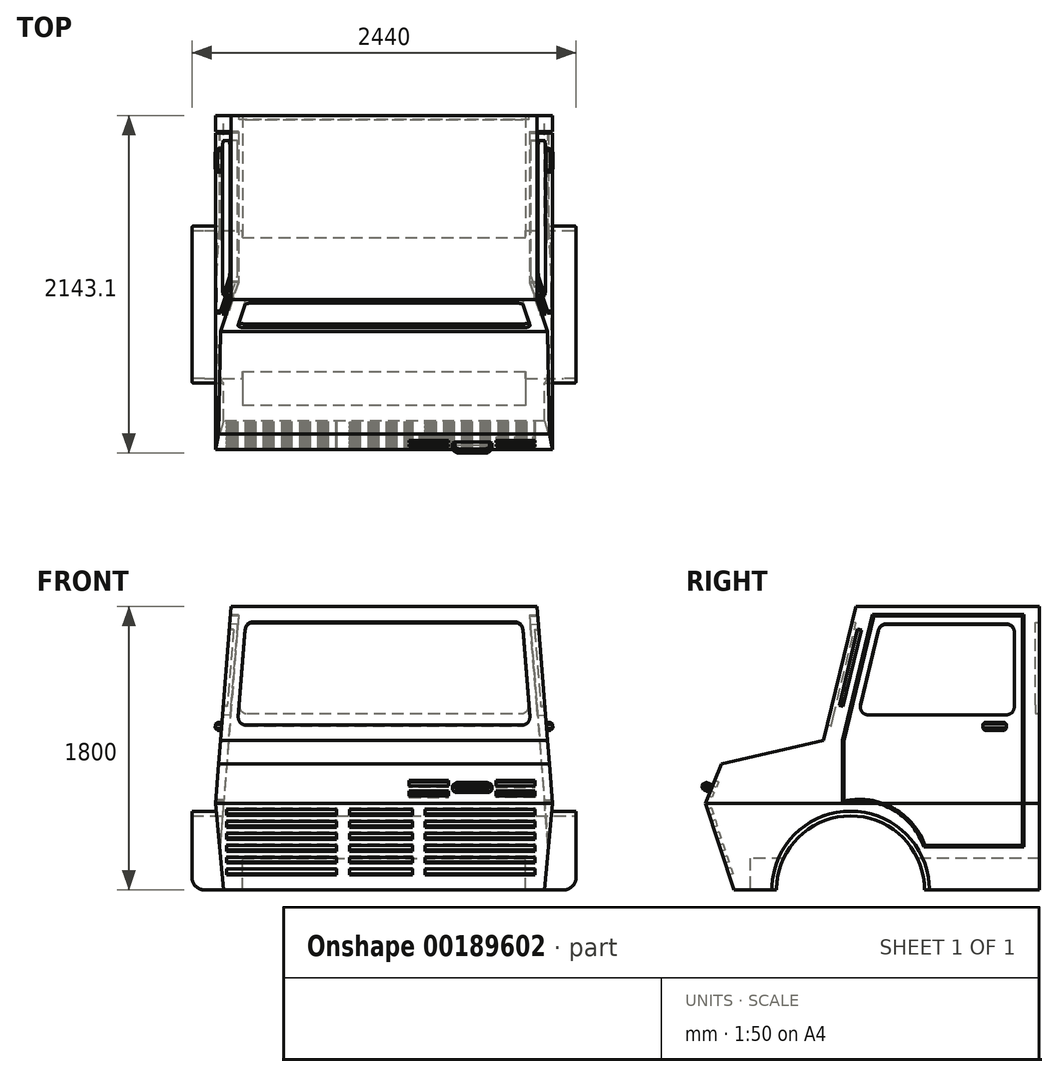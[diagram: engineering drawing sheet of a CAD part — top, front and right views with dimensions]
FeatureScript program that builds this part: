
annotation { "Feature Type Name" : "Feature", "Feature Type Description" : "" }
export const myFeature = defineFeature(function(context is Context, id is Id, definition is map)
    precondition{}
    {
        {
            var Q0;
            Q0=qCreatedBy(makeId("Right.planeOp"),FACE);
            var sketch = newSketch(context, id + "F0", { "sketchPlane" : qUnion([Q0])});
            skLineSegment(sketch, "E0", {"start": v(-687.2, -888.86) * mm, "end": v(-447.2, -888.86) * mm});
            skLineSegment(sketch, "E1", {"start": v(1252.8, -888.86) * mm, "end": v(1252.8, 911.14) * mm});
            skLineSegment(sketch, "E2", {"start": v(1252.8, 911.14) * mm, "end": v(86.04, 911.14) * mm});
            skLineSegment(sketch, "E3", {"start": v(86.04, 911.14) * mm, "end": v(-118.03, 61.14) * mm});
            skLineSegment(sketch, "E4", {"start": v(-118.03, 61.14) * mm, "end": v(-768.03, -88.86) * mm});
            skLineSegment(sketch, "E5", {"start": v(-768.03, -88.86) * mm, "end": v(-868.03, -338.86) * mm});
            skLineSegment(sketch, "E6", {"start": v(-868.03, -338.86) * mm, "end": v(-687.2, -888.86) * mm});
            skArc(sketch, "E7", {"start": v(552.8, -888.86) * mm, "mid": v(52.8, -388.86) * mm, "end": v(-447.2, -888.86) * mm});
            skLineSegment(sketch, "E8.trimOffspring", {"start": v(552.8, -888.86) * mm, "end": v(1252.8, -888.86) * mm});
            skLineSegment(sketch, "E9", {"start": v(-687.2, -888.86) * mm, "end": v(-687.2, 1285.93) * mm, "construction": true});
            skSolve(sketch);
        }
        {
            var Q0;
            Q0 = qSketchRegion(id + "F0", true);
            extrude(context, id + "F1", {"entities" : qUnion([Q0]), "depth" : 2140 * mm});
        }
        {
            var Q0;
            Q0=makeQuery(id+"F1.opExtrude","SWEPT_FACE",FACE,{"disambiguationData":[OSD([sQuery(id+"F0.wireOp",EDGE,"E1")])]});
            var sketch = newSketch(context, id + "F2", { "sketchPlane" : qUnion([Q0])});
            skLineSegment(sketch, "E10", {"start": v(-2140, -888.86) * mm, "end": v(-2090, -888.86) * mm});
            skLineSegment(sketch, "E11", {"start": v(-2090, -888.86) * mm, "end": v(-2140, -338.86) * mm});
            skLineSegment(sketch, "E12", {"start": v(-2140, -338.86) * mm, "end": v(-2040, 911.14) * mm});
            skLineSegment(sketch, "E13", {"start": v(-2040, 911.14) * mm, "end": v(-2140, 911.14) * mm});
            skLineSegment(sketch, "E14", {"start": v(-2140, 911.14) * mm, "end": v(-2140, -888.86) * mm});
            skLineSegment(sketch, "E15", {"start": v(-2090, -888.86) * mm, "end": v(-2140, -888.86) * mm});
            skLineSegment(sketch, "E16", {"start": v(0, -888.86) * mm, "end": v(-50, -888.86) * mm});
            skLineSegment(sketch, "E17", {"start": v(-50, -888.86) * mm, "end": v(0, -338.86) * mm});
            skLineSegment(sketch, "E18", {"start": v(0, -338.86) * mm, "end": v(-100, 911.14) * mm});
            skLineSegment(sketch, "E19", {"start": v(-100, 911.14) * mm, "end": v(0, 911.14) * mm});
            skLineSegment(sketch, "E20", {"start": v(0, 911.14) * mm, "end": v(0, -888.86) * mm});
            skSolve(sketch);
        }
        {
            var Q0;
            {var subQ0=sQuery(id+"F2.wireOp",EDGE,"E12");Q0=makeQuery(id+"F2.imprint","IMPRINT",FACE,{"disambiguationData":[TD([[makeQuery(id+"F2.imprint","IMPRINT",EDGE,{"derivedFrom":subQ0}),1.0]])]});}
            var Q1;
            {var subQ0=sQuery(id+"F2.wireOp",EDGE,"E11");Q1=makeQuery(id+"F2.imprint","IMPRINT",FACE,{"disambiguationData":[TD([[makeQuery(id+"F2.imprint","IMPRINT",EDGE,{"derivedFrom":subQ0}),1.0]])]});}
            var Q2;
            {var subQ0=sQuery(id+"F2.wireOp",EDGE,"E16");Q2=makeQuery(id+"F2.imprint","IMPRINT",FACE,{"disambiguationData":[TD([[makeQuery(id+"F2.imprint","IMPRINT",EDGE,{"derivedFrom":subQ0}),1.0]])]});}
            var Q3;
            {var subQ0=sQuery(id+"F2.wireOp",EDGE,"E18");Q3=makeQuery(id+"F2.imprint","IMPRINT",FACE,{"disambiguationData":[TD([[makeQuery(id+"F2.imprint","IMPRINT",EDGE,{"derivedFrom":subQ0}),-1.0]])]});}
            extrude(context, id + "F3", {"entities" : qUnion([Q0, Q1, Q2, Q3]), "operationType" : NewBodyOperationType.REMOVE, "oppositeDirection" : true, "depth" : 2500 * mm});
        }
        {
            var Q0;
            Q0=makeQuery(id+"F1.opExtrude","SWEPT_FACE",FACE,{"disambiguationData":[OSD([sQuery(id+"F0.wireOp",EDGE,"E6")])]});
            var sketch = newSketch(context, id + "F4", { "sketchPlane" : qUnion([Q0])});
            skLineSegment(sketch, "E21.bottom", {"start": v(70, -90.81) * mm, "end": v(770, -90.81) * mm});
            skLineSegment(sketch, "E21.top", {"start": v(70, -130.81) * mm, "end": v(770, -130.81) * mm});
            skLineSegment(sketch, "E21.left", {"start": v(70, -90.81) * mm, "end": v(70, -130.81) * mm});
            skLineSegment(sketch, "E21.right", {"start": v(770, -90.81) * mm, "end": v(770, -130.81) * mm});
            skLineSegment(sketch, "E22.bottom", {"start": v(850, -90.81) * mm, "end": v(1250, -90.81) * mm});
            skLineSegment(sketch, "E22.top", {"start": v(850, -130.81) * mm, "end": v(1250, -130.81) * mm});
            skLineSegment(sketch, "E22.left", {"start": v(850, -90.81) * mm, "end": v(850, -130.81) * mm});
            skLineSegment(sketch, "E22.right", {"start": v(1250, -90.81) * mm, "end": v(1250, -130.81) * mm});
            skLineSegment(sketch, "E23.bottom", {"start": v(1330, -90.81) * mm, "end": v(2030, -90.81) * mm});
            skLineSegment(sketch, "E23.top", {"start": v(1330, -130.81) * mm, "end": v(2030, -130.81) * mm});
            skLineSegment(sketch, "E23.left", {"start": v(1330, -90.81) * mm, "end": v(1330, -130.81) * mm});
            skLineSegment(sketch, "E23.right", {"start": v(2030, -90.81) * mm, "end": v(2030, -130.81) * mm});
            skLineSegment(sketch, "E24.bottom", {"start": v(70, -170.81) * mm, "end": v(770, -170.81) * mm});
            skLineSegment(sketch, "E24.top", {"start": v(70, -210.81) * mm, "end": v(770, -210.81) * mm});
            skLineSegment(sketch, "E24.left", {"start": v(70, -170.81) * mm, "end": v(70, -210.81) * mm});
            skLineSegment(sketch, "E24.right", {"start": v(770, -170.81) * mm, "end": v(770, -210.81) * mm});
            skLineSegment(sketch, "E25.bottom", {"start": v(850, -170.81) * mm, "end": v(1250, -170.81) * mm});
            skLineSegment(sketch, "E25.top", {"start": v(850, -210.81) * mm, "end": v(1250, -210.81) * mm});
            skLineSegment(sketch, "E25.left", {"start": v(850, -170.81) * mm, "end": v(850, -210.81) * mm});
            skLineSegment(sketch, "E25.right", {"start": v(1250, -170.81) * mm, "end": v(1250, -210.81) * mm});
            skLineSegment(sketch, "E26.bottom", {"start": v(1330, -170.81) * mm, "end": v(2030, -170.81) * mm});
            skLineSegment(sketch, "E26.top", {"start": v(1330, -210.81) * mm, "end": v(2030, -210.81) * mm});
            skLineSegment(sketch, "E26.left", {"start": v(1330, -170.81) * mm, "end": v(1330, -210.81) * mm});
            skLineSegment(sketch, "E26.right", {"start": v(2030, -170.81) * mm, "end": v(2030, -210.81) * mm});
            skLineSegment(sketch, "E27.bottom", {"start": v(70, -250.81) * mm, "end": v(770, -250.81) * mm});
            skLineSegment(sketch, "E27.top", {"start": v(70, -290.81) * mm, "end": v(770, -290.81) * mm});
            skLineSegment(sketch, "E27.left", {"start": v(70, -250.81) * mm, "end": v(70, -290.81) * mm});
            skLineSegment(sketch, "E27.right", {"start": v(770, -250.81) * mm, "end": v(770, -290.81) * mm});
            skLineSegment(sketch, "E28.bottom", {"start": v(850, -250.81) * mm, "end": v(1250, -250.81) * mm});
            skLineSegment(sketch, "E28.top", {"start": v(850, -290.81) * mm, "end": v(1250, -290.81) * mm});
            skLineSegment(sketch, "E28.left", {"start": v(850, -250.81) * mm, "end": v(850, -290.81) * mm});
            skLineSegment(sketch, "E28.right", {"start": v(1250, -250.81) * mm, "end": v(1250, -290.81) * mm});
            skLineSegment(sketch, "E29.bottom", {"start": v(1330, -250.81) * mm, "end": v(2030, -250.81) * mm});
            skLineSegment(sketch, "E29.top", {"start": v(1330, -290.81) * mm, "end": v(2030, -290.81) * mm});
            skLineSegment(sketch, "E29.left", {"start": v(1330, -250.81) * mm, "end": v(1330, -290.81) * mm});
            skLineSegment(sketch, "E29.right", {"start": v(2030, -250.81) * mm, "end": v(2030, -290.81) * mm});
            skLineSegment(sketch, "E30.bottom", {"start": v(70, -330.81) * mm, "end": v(770, -330.81) * mm});
            skLineSegment(sketch, "E30.top", {"start": v(70, -370.81) * mm, "end": v(770, -370.81) * mm});
            skLineSegment(sketch, "E30.left", {"start": v(70, -330.81) * mm, "end": v(70, -370.81) * mm});
            skLineSegment(sketch, "E30.right", {"start": v(770, -330.81) * mm, "end": v(770, -370.81) * mm});
            skLineSegment(sketch, "E31.bottom", {"start": v(850, -330.81) * mm, "end": v(1250, -330.81) * mm});
            skLineSegment(sketch, "E31.top", {"start": v(850, -370.81) * mm, "end": v(1250, -370.81) * mm});
            skLineSegment(sketch, "E31.left", {"start": v(850, -330.81) * mm, "end": v(850, -370.81) * mm});
            skLineSegment(sketch, "E31.right", {"start": v(1250, -330.81) * mm, "end": v(1250, -370.81) * mm});
            skLineSegment(sketch, "E32.bottom", {"start": v(1330, -330.81) * mm, "end": v(2030, -330.81) * mm});
            skLineSegment(sketch, "E32.top", {"start": v(1330, -370.81) * mm, "end": v(2030, -370.81) * mm});
            skLineSegment(sketch, "E32.left", {"start": v(1330, -330.81) * mm, "end": v(1330, -370.81) * mm});
            skLineSegment(sketch, "E32.right", {"start": v(2030, -330.81) * mm, "end": v(2030, -370.81) * mm});
            skLineSegment(sketch, "E33.bottom", {"start": v(70, -410.81) * mm, "end": v(770, -410.81) * mm});
            skLineSegment(sketch, "E33.top", {"start": v(70, -450.81) * mm, "end": v(770, -450.81) * mm});
            skLineSegment(sketch, "E33.left", {"start": v(70, -410.81) * mm, "end": v(70, -450.81) * mm});
            skLineSegment(sketch, "E33.right", {"start": v(770, -410.81) * mm, "end": v(770, -450.81) * mm});
            skLineSegment(sketch, "E34.bottom", {"start": v(850, -410.81) * mm, "end": v(1250, -410.81) * mm});
            skLineSegment(sketch, "E34.top", {"start": v(850, -450.81) * mm, "end": v(1250, -450.81) * mm});
            skLineSegment(sketch, "E34.left", {"start": v(850, -410.81) * mm, "end": v(850, -450.81) * mm});
            skLineSegment(sketch, "E34.right", {"start": v(1250, -410.81) * mm, "end": v(1250, -450.81) * mm});
            skLineSegment(sketch, "E35.bottom", {"start": v(1330, -410.81) * mm, "end": v(2030, -410.81) * mm});
            skLineSegment(sketch, "E35.top", {"start": v(1330, -450.81) * mm, "end": v(2030, -450.81) * mm});
            skLineSegment(sketch, "E35.left", {"start": v(1330, -410.81) * mm, "end": v(1330, -450.81) * mm});
            skLineSegment(sketch, "E35.right", {"start": v(2030, -410.81) * mm, "end": v(2030, -450.81) * mm});
            skLineSegment(sketch, "E36.bottom", {"start": v(70, -490.81) * mm, "end": v(770, -490.81) * mm});
            skLineSegment(sketch, "E36.top", {"start": v(70, -530.81) * mm, "end": v(770, -530.81) * mm});
            skLineSegment(sketch, "E36.left", {"start": v(70, -490.81) * mm, "end": v(70, -530.81) * mm});
            skLineSegment(sketch, "E36.right", {"start": v(770, -490.81) * mm, "end": v(770, -530.81) * mm});
            skLineSegment(sketch, "E37.bottom", {"start": v(850, -490.81) * mm, "end": v(1250, -490.81) * mm});
            skLineSegment(sketch, "E37.top", {"start": v(850, -530.81) * mm, "end": v(1250, -530.81) * mm});
            skLineSegment(sketch, "E37.left", {"start": v(850, -490.81) * mm, "end": v(850, -530.81) * mm});
            skLineSegment(sketch, "E37.right", {"start": v(1250, -490.81) * mm, "end": v(1250, -530.81) * mm});
            skLineSegment(sketch, "E38.bottom", {"start": v(1330, -490.81) * mm, "end": v(2030, -490.81) * mm});
            skLineSegment(sketch, "E38.top", {"start": v(1330, -530.81) * mm, "end": v(2030, -530.81) * mm});
            skLineSegment(sketch, "E38.left", {"start": v(1330, -490.81) * mm, "end": v(1330, -530.81) * mm});
            skLineSegment(sketch, "E38.right", {"start": v(2030, -490.81) * mm, "end": v(2030, -530.81) * mm});
            skSolve(sketch);
        }
        {
            var Q0;
            Q0=makeQuery(id+"F4.imprint","IMPRINT",FACE,{"disambiguationData":[TD([[makeQuery(id+"F4.imprint","IMPRINT",EDGE,{"derivedFrom":sQuery(id+"F4.wireOp",EDGE,"E22.bottom")}),-1.0]])]});
            var Q1;
            Q1=makeQuery(id+"F4.imprint","IMPRINT",FACE,{"disambiguationData":[TD([[makeQuery(id+"F4.imprint","IMPRINT",EDGE,{"derivedFrom":sQuery(id+"F4.wireOp",EDGE,"E23.bottom")}),-1.0]])]});
            var Q2;
            Q2=makeQuery(id+"F4.imprint","IMPRINT",FACE,{"disambiguationData":[TD([[makeQuery(id+"F4.imprint","IMPRINT",EDGE,{"derivedFrom":sQuery(id+"F4.wireOp",EDGE,"E26.bottom")}),-1.0]])]});
            var Q3;
            Q3=makeQuery(id+"F4.imprint","IMPRINT",FACE,{"disambiguationData":[TD([[makeQuery(id+"F4.imprint","IMPRINT",EDGE,{"derivedFrom":sQuery(id+"F4.wireOp",EDGE,"E25.bottom")}),-1.0]])]});
            var Q4;
            Q4=makeQuery(id+"F4.imprint","IMPRINT",FACE,{"disambiguationData":[TD([[makeQuery(id+"F4.imprint","IMPRINT",EDGE,{"derivedFrom":sQuery(id+"F4.wireOp",EDGE,"E24.bottom")}),-1.0]])]});
            var Q5;
            Q5=makeQuery(id+"F4.imprint","IMPRINT",FACE,{"disambiguationData":[TD([[makeQuery(id+"F4.imprint","IMPRINT",EDGE,{"derivedFrom":sQuery(id+"F4.wireOp",EDGE,"E21.bottom")}),-1.0]])]});
            var Q6;
            Q6=makeQuery(id+"F4.imprint","IMPRINT",FACE,{"disambiguationData":[TD([[makeQuery(id+"F4.imprint","IMPRINT",EDGE,{"derivedFrom":sQuery(id+"F4.wireOp",EDGE,"E27.bottom")}),-1.0]])]});
            var Q7;
            Q7=makeQuery(id+"F4.imprint","IMPRINT",FACE,{"disambiguationData":[TD([[makeQuery(id+"F4.imprint","IMPRINT",EDGE,{"derivedFrom":sQuery(id+"F4.wireOp",EDGE,"E28.bottom")}),-1.0]])]});
            var Q8;
            Q8=makeQuery(id+"F4.imprint","IMPRINT",FACE,{"disambiguationData":[TD([[makeQuery(id+"F4.imprint","IMPRINT",EDGE,{"derivedFrom":sQuery(id+"F4.wireOp",EDGE,"E29.bottom")}),-1.0]])]});
            var Q9;
            Q9=makeQuery(id+"F4.imprint","IMPRINT",FACE,{"disambiguationData":[TD([[makeQuery(id+"F4.imprint","IMPRINT",EDGE,{"derivedFrom":sQuery(id+"F4.wireOp",EDGE,"E32.bottom")}),-1.0]])]});
            var Q10;
            Q10=makeQuery(id+"F4.imprint","IMPRINT",FACE,{"disambiguationData":[TD([[makeQuery(id+"F4.imprint","IMPRINT",EDGE,{"derivedFrom":sQuery(id+"F4.wireOp",EDGE,"E31.bottom")}),-1.0]])]});
            var Q11;
            Q11=makeQuery(id+"F4.imprint","IMPRINT",FACE,{"disambiguationData":[TD([[makeQuery(id+"F4.imprint","IMPRINT",EDGE,{"derivedFrom":sQuery(id+"F4.wireOp",EDGE,"E30.bottom")}),-1.0]])]});
            var Q12;
            Q12=makeQuery(id+"F4.imprint","IMPRINT",FACE,{"disambiguationData":[TD([[makeQuery(id+"F4.imprint","IMPRINT",EDGE,{"derivedFrom":sQuery(id+"F4.wireOp",EDGE,"E33.bottom")}),-1.0]])]});
            var Q13;
            Q13=makeQuery(id+"F4.imprint","IMPRINT",FACE,{"disambiguationData":[TD([[makeQuery(id+"F4.imprint","IMPRINT",EDGE,{"derivedFrom":sQuery(id+"F4.wireOp",EDGE,"E34.bottom")}),-1.0]])]});
            var Q14;
            Q14=makeQuery(id+"F4.imprint","IMPRINT",FACE,{"disambiguationData":[TD([[makeQuery(id+"F4.imprint","IMPRINT",EDGE,{"derivedFrom":sQuery(id+"F4.wireOp",EDGE,"E35.bottom")}),-1.0]])]});
            var Q15;
            Q15=makeQuery(id+"F4.imprint","IMPRINT",FACE,{"disambiguationData":[TD([[makeQuery(id+"F4.imprint","IMPRINT",EDGE,{"derivedFrom":sQuery(id+"F4.wireOp",EDGE,"E37.bottom")}),-1.0]])]});
            var Q16;
            Q16=makeQuery(id+"F4.imprint","IMPRINT",FACE,{"disambiguationData":[TD([[makeQuery(id+"F4.imprint","IMPRINT",EDGE,{"derivedFrom":sQuery(id+"F4.wireOp",EDGE,"E38.bottom")}),-1.0]])]});
            var Q17;
            Q17=makeQuery(id+"F4.imprint","IMPRINT",FACE,{"disambiguationData":[TD([[makeQuery(id+"F4.imprint","IMPRINT",EDGE,{"derivedFrom":sQuery(id+"F4.wireOp",EDGE,"E36.bottom")}),-1.0]])]});
            extrude(context, id + "F5", {"entities" : qUnion([Q0, Q1, Q2, Q3, Q4, Q5, Q6, Q7, Q8, Q9, Q10, Q11, Q12, Q13, Q14, Q15, Q16, Q17]), "operationType" : NewBodyOperationType.REMOVE, "oppositeDirection" : true, "depth" : 25 * mm});
        }
        {
            var Q0;
            Q0=makeQuery(id+"F1.opExtrude","SWEPT_FACE",FACE,{"disambiguationData":[OSD([sQuery(id+"F0.wireOp",EDGE,"E3")])]});
            var sketch = newSketch(context, id + "F6", { "sketchPlane" : qUnion([Q0])});
            skLineSegment(sketch, "E39", {"start": v(188.94, 759.93) * mm, "end": v(144.27, 185.78) * mm});
            skLineSegment(sketch, "E40", {"start": v(194.12, 131.9) * mm, "end": v(1945.88, 131.9) * mm});
            skLineSegment(sketch, "E41", {"start": v(1995.73, 185.78) * mm, "end": v(1951.06, 759.93) * mm});
            skLineSegment(sketch, "E42", {"start": v(1901.22, 806.05) * mm, "end": v(238.78, 806.05) * mm});
            skPoint(sketch, "E43.visualSharp", {"position": v(140.08, 131.9) * mm});
            skArc(sketch, "E43.filletArc", {"start": v(144.27, 185.78) * mm, "mid": v(157.42, 147.94) * mm, "end": v(194.12, 131.9) * mm});
            skPoint(sketch, "E44.visualSharp", {"position": v(1999.92, 131.9) * mm});
            skArc(sketch, "E44.filletArc", {"start": v(1945.88, 131.9) * mm, "mid": v(1982.58, 147.94) * mm, "end": v(1995.73, 185.78) * mm});
            skPoint(sketch, "E45.visualSharp", {"position": v(1947.48, 806.05) * mm});
            skArc(sketch, "E45.filletArc", {"start": v(1951.06, 759.93) * mm, "mid": v(1935.17, 792.75) * mm, "end": v(1901.22, 806.05) * mm});
            skPoint(sketch, "E46.visualSharp", {"position": v(192.52, 806.05) * mm});
            skArc(sketch, "E46.filletArc", {"start": v(238.78, 806.05) * mm, "mid": v(204.83, 792.75) * mm, "end": v(188.94, 759.93) * mm});
            skSolve(sketch);
        }
        {
            var Q0;
            Q0=makeQuery(id+"F6.imprint","IMPRINT",FACE,{"disambiguationData":[TD([[makeQuery(id+"F6.imprint","IMPRINT",EDGE,{"derivedFrom":sQuery(id+"F6.wireOp",EDGE,"6I6eG5J9-oO44-mDBK-8rPG-g7Z5jDPBqrvn")}),-1.0]])]});
            var Q1;
            Q1=makeQuery(id+"F6.imprint","IMPRINT",FACE,{"disambiguationData":[TD([[makeQuery(id+"F6.imprint","IMPRINT",EDGE,{"derivedFrom":sQuery(id+"F6.wireOp",EDGE,"E39")}),1.0]])]});
            extrude(context, id + "F7", {"entities" : qUnion([Q0, Q1]), "operationType" : NewBodyOperationType.REMOVE, "oppositeDirection" : true, "depth" : 25 * mm});
        }
        {
            var Q0;
            Q0=makeQuery(id+"F3.boolean.opBoolean","COPY",FACE,{"derivedFrom":makeQuery(id+"F3.opExtrude","SWEPT_FACE",FACE,{"disambiguationData":[OSD([sQuery(id+"F2.wireOp",EDGE,"E12")])]})});
            var sketch = newSketch(context, id + "F8", { "sketchPlane" : qUnion([Q0])});
            skLineSegment(sketch, "E47", {"start": v(1152.8, 695.56) * mm, "end": v(192.4, 695.56) * mm});
            skLineSegment(sketch, "E48", {"start": v(192.4, 695.56) * mm, "end": v(0, -108.43) * mm});
            skLineSegment(sketch, "E49", {"start": v(0, -108.43) * mm, "end": v(0, -508.43) * mm});
            skArc(sketch, "E50", {"start": v(517.8, -782.7) * mm, "mid": v(312.84, -543.72) * mm, "end": v(0, -508.43) * mm});
            skLineSegment(sketch, "E51", {"start": v(517.8, -782.7) * mm, "end": v(1152.8, -782.7) * mm});
            skLineSegment(sketch, "E52", {"start": v(1152.8, 695.56) * mm, "end": v(1152.8, -782.7) * mm});
            skLineSegment(sketch, "E53", {"start": v(1142.8, 685.56) * mm, "end": v(200.3, 685.56) * mm});
            skLineSegment(sketch, "E54", {"start": v(200.3, 685.56) * mm, "end": v(10, -109.61) * mm});
            skLineSegment(sketch, "E55", {"start": v(10, -109.61) * mm, "end": v(10, -495.6) * mm});
            skArc(sketch, "E56", {"start": v(524.84, -772.7) * mm, "mid": v(320.1, -536.26) * mm, "end": v(10, -495.6) * mm});
            skLineSegment(sketch, "E57", {"start": v(524.84, -772.7) * mm, "end": v(1142.8, -772.7) * mm});
            skLineSegment(sketch, "E58", {"start": v(1142.8, 685.56) * mm, "end": v(1142.8, -772.7) * mm});
            skPoint(sketch, "E59.visualSharp", {"position": v(-103.75, -97.36) * mm});
            skLineSegment(sketch, "E60", {"start": v(1042.8, 635.56) * mm, "end": v(279.18, 635.56) * mm});
            skLineSegment(sketch, "E61", {"start": v(230.56, 597.2) * mm, "end": v(115.69, 117.2) * mm});
            skLineSegment(sketch, "E62", {"start": v(164.32, 55.56) * mm, "end": v(1042.8, 55.56) * mm});
            skLineSegment(sketch, "E63", {"start": v(1092.8, 105.56) * mm, "end": v(1092.8, 585.56) * mm});
            skPoint(sketch, "E64.visualSharp", {"position": v(239.74, 635.56) * mm});
            skArc(sketch, "E64.filletArc", {"start": v(279.18, 635.56) * mm, "mid": v(248.22, 624.81) * mm, "end": v(230.56, 597.2) * mm});
            skPoint(sketch, "E65.visualSharp", {"position": v(100.94, 55.56) * mm});
            skArc(sketch, "E65.filletArc", {"start": v(115.69, 117.2) * mm, "mid": v(125.06, 74.6) * mm, "end": v(164.32, 55.56) * mm});
            skPoint(sketch, "E66.visualSharp", {"position": v(1092.8, 55.56) * mm});
            skArc(sketch, "E66.filletArc", {"start": v(1042.8, 55.56) * mm, "mid": v(1078.15, 70.2) * mm, "end": v(1092.8, 105.56) * mm});
            skPoint(sketch, "E67.visualSharp", {"position": v(1092.8, 635.56) * mm});
            skArc(sketch, "E67.filletArc", {"start": v(1092.8, 585.56) * mm, "mid": v(1078.15, 620.92) * mm, "end": v(1042.8, 635.56) * mm});
            skSolve(sketch);
        }
        {
            var Q0;
            {var subQ9=sQuery(id+"F8.wireOp",EDGE,"E47");Q0=makeQuery(id+"F8.imprint","IMPRINT",FACE,{"disambiguationData":[TD([[makeQuery(id+"F8.imprint","IMPRINT",EDGE,{"derivedFrom":subQ9}),1.0]])]});}
            var Q1;
            {var subQ1=sQuery(id+"F8.wireOp",EDGE,"E51");Q1=makeQuery(id+"F8.imprint","IMPRINT",FACE,{"disambiguationData":[TD([[makeQuery(id+"F8.imprint","IMPRINT",EDGE,{"derivedFrom":subQ1}),1.0]])]});}
            var Q2;
            Q2=makeQuery(id+"F8.imprint","IMPRINT",FACE,{"disambiguationData":[TD([[makeQuery(id+"F8.imprint","IMPRINT",EDGE,{"derivedFrom":sQuery(id+"F8.wireOp",EDGE,"RXpK4xbC-jTpL-yFPa-w4cw-NWwqhQofK6yF")}),1.0]])]});
            var Q3;
            Q3=makeQuery(id+"F8.imprint","IMPRINT",FACE,{"disambiguationData":[TD([[makeQuery(id+"F8.imprint","IMPRINT",EDGE,{"derivedFrom":sQuery(id+"F8.wireOp",EDGE,"E60")}),1.0]])]});
            extrude(context, id + "F9", {"entities" : qUnion([Q0, Q1, Q2, Q3]), "operationType" : NewBodyOperationType.REMOVE, "oppositeDirection" : true, "depth" : 50 * mm});
        }
        {
            var Q0;
            Q0=makeQuery(id+"F3.boolean.opBoolean","COPY",FACE,{"derivedFrom":makeQuery(id+"F3.opExtrude","SWEPT_FACE",FACE,{"disambiguationData":[OSD([sQuery(id+"F2.wireOp",EDGE,"E18")])]})});
            var sketch = newSketch(context, id + "F10", { "sketchPlane" : qUnion([Q0])});
            skLineSegment(sketch, "E68.MirrorCS", {"start": v(-517.74, -612.04) * mm, "end": v(-1152.8, -612.04) * mm});
            skLineSegment(sketch, "E69.MirrorCS", {"start": v(-1152.8, 866.21) * mm, "end": v(-1152.8, -612.04) * mm});
            skLineSegment(sketch, "E70.MirrorCS", {"start": v(-1142.8, 856.21) * mm, "end": v(-200.2, 856.21) * mm});
            skLineSegment(sketch, "E71.MirrorCS", {"start": v(-200.2, 856.21) * mm, "end": v(-9.92, 61.04) * mm});
            skLineSegment(sketch, "E72.MirrorCS", {"start": v(-9.92, 61.04) * mm, "end": v(-9.92, -324.94) * mm});
            skArc(sketch, "E73.MirrorCS", {"start": v(-524.8, -602.04) * mm, "mid": v(-320.04, -365.6) * mm, "end": v(-9.92, -324.94) * mm});
            skLineSegment(sketch, "E74.MirrorCS", {"start": v(-524.8, -602.04) * mm, "end": v(-1142.8, -602.04) * mm});
            skLineSegment(sketch, "E75.MirrorCS", {"start": v(-1142.8, 856.21) * mm, "end": v(-1142.8, -602.04) * mm});
            skPoint(sketch, "E76.MirrorP", {"position": v(142.86, 102.71) * mm});
            skLineSegment(sketch, "E77.MirrorCS", {"start": v(-1152.8, 866.21) * mm, "end": v(-192.32, 866.21) * mm});
            skLineSegment(sketch, "E78.MirrorCS", {"start": v(-192.32, 866.21) * mm, "end": v(0.08, 62.22) * mm});
            skLineSegment(sketch, "E79.MirrorCS", {"start": v(0.08, 62.22) * mm, "end": v(0.08, -337.78) * mm});
            skArc(sketch, "E80.MirrorCS", {"start": v(-517.74, -612.04) * mm, "mid": v(-312.77, -373.05) * mm, "end": v(0.08, -337.78) * mm});
            skLineSegment(sketch, "E81", {"start": v(-1092.8, 756.21) * mm, "end": v(-1092.8, 276.21) * mm});
            skLineSegment(sketch, "E82", {"start": v(-1042.8, 226.21) * mm, "end": v(-164.23, 226.21) * mm});
            skLineSegment(sketch, "E83", {"start": v(-115.6, 287.85) * mm, "end": v(-230.47, 767.85) * mm});
            skLineSegment(sketch, "E84", {"start": v(-279.1, 806.21) * mm, "end": v(-1042.8, 806.21) * mm});
            skPoint(sketch, "E85.visualSharp", {"position": v(-1092.8, 806.21) * mm});
            skArc(sketch, "E85.filletArc", {"start": v(-1042.8, 806.21) * mm, "mid": v(-1078.15, 791.57) * mm, "end": v(-1092.8, 756.21) * mm});
            skPoint(sketch, "E86.visualSharp", {"position": v(-239.65, 806.21) * mm});
            skArc(sketch, "E86.filletArc", {"start": v(-230.47, 767.85) * mm, "mid": v(-248.13, 795.47) * mm, "end": v(-279.1, 806.21) * mm});
            skPoint(sketch, "E87.visualSharp", {"position": v(-1092.8, 226.21) * mm});
            skArc(sketch, "E87.filletArc", {"start": v(-1092.8, 276.21) * mm, "mid": v(-1078.15, 240.86) * mm, "end": v(-1042.8, 226.21) * mm});
            skPoint(sketch, "E88.visualSharp", {"position": v(-100.86, 226.21) * mm});
            skArc(sketch, "E88.filletArc", {"start": v(-164.23, 226.21) * mm, "mid": v(-124.98, 245.25) * mm, "end": v(-115.6, 287.85) * mm});
            skSolve(sketch);
        }
        {
            var Q0;
            Q0 = qSketchRegion(id + "F10", true);
            var Q1;
            Q1=makeQuery(id+"F10.imprint","IMPRINT",FACE,{"disambiguationData":[TD([[makeQuery(id+"F10.imprint","IMPRINT",EDGE,{"derivedFrom":sQuery(id+"F10.wireOp",EDGE,"E81")}),1.0]])]});
            extrude(context, id + "F11", {"entities" : qUnion([Q0, Q1]), "operationType" : NewBodyOperationType.REMOVE, "oppositeDirection" : true, "depth" : 50 * mm});
        }
        {
            var Q0;
            Q0=qCreatedBy(makeId("Right.planeOp"),FACE);
            var sketch = newSketch(context, id + "F12", { "sketchPlane" : qUnion([Q0])});
            skArc(sketch, "E89", {"start": v(552.8, -888.86) * mm, "mid": v(52.8, -388.86) * mm, "end": v(-447.2, -888.86) * mm});
            skArc(sketch, "E90", {"start": v(522.8, -888.86) * mm, "mid": v(52.8, -418.86) * mm, "end": v(-417.2, -888.86) * mm});
            skLineSegment(sketch, "E91", {"start": v(1160.67, -888.86) * mm, "end": v(-584.2, -888.86) * mm, "construction": true});
            skLineSegment(sketch, "E92", {"start": v(552.8, -888.86) * mm, "end": v(522.8, -888.86) * mm});
            skLineSegment(sketch, "E93", {"start": v(-417.2, -888.86) * mm, "end": v(-447.2, -888.86) * mm});
            skSolve(sketch);
        }
        {
            var Q0;
            Q0=makeQuery(id+"F12.imprint","IMPRINT",FACE,{"disambiguationData":[TD([[makeQuery(id+"F12.imprint","IMPRINT",EDGE,{"derivedFrom":sQuery(id+"F12.wireOp",EDGE,"E89")}),1.0]])]});
            extrude(context, id + "F13", {"entities" : qUnion([Q0]), "operationType" : NewBodyOperationType.ADD, "oppositeDirection" : true, "depth" : 150 * mm, "hasSecondDirection" : true, "secondDirectionOppositeDirection" : false, "secondDirectionDepth" : 2290 * mm});
        }
        {
            var Q0;
            Q0=makeQuery(id+"F13.opExtrude","CAP_EDGE",EDGE,{"disambiguationData":[OSD([sQuery(id+"F12.wireOp",EDGE,"E93")])],"isStart":false});
            var Q1;
            Q1=makeQuery(id+"F13.opExtrude","CAP_EDGE",EDGE,{"disambiguationData":[OSD([sQuery(id+"F12.wireOp",EDGE,"E92")])],"isStart":false});
            var Q2;
            Q2=makeQuery(id+"F13.opExtrude","CAP_EDGE",EDGE,{"disambiguationData":[OSD([sQuery(id+"F12.wireOp",EDGE,"E93")])],"isStart":true});
            var Q3;
            Q3=makeQuery(id+"F13.opExtrude","CAP_EDGE",EDGE,{"disambiguationData":[OSD([sQuery(id+"F12.wireOp",EDGE,"E92")])],"isStart":true});
            var Q4;
            Q4=makeQuery(id+"F3.boolean.opBoolean","COPY",EDGE,{"derivedFrom":makeQuery(id+"F3.opExtrude","SWEPT_EDGE",EDGE,{"disambiguationData":[OSD([sQuery(id+"F0.wireOp",EDGE,"E1"),sQuery(id+"F0.wireOp",EDGE,"E2"),sQuery(id+"F2.wireOp",EDGE,"E12"),sQuery(id+"F2.wireOp",EDGE,"E13")])]})});
            var Q5;
            Q5=makeQuery(id+"F3.boolean.opBoolean","COPY",EDGE,{"derivedFrom":makeQuery(id+"F3.opExtrude","SWEPT_EDGE",EDGE,{"disambiguationData":[OSD([sQuery(id+"F0.wireOp",EDGE,"E1"),sQuery(id+"F0.wireOp",EDGE,"E2"),sQuery(id+"F2.wireOp",EDGE,"E18"),sQuery(id+"F2.wireOp",EDGE,"E19")])]})});
            fillet(context, id + "F14", {"entities" : qUnion([Q0, Q1, Q2, Q3, Q4, Q5]), "radius" : 80 * mm, "tangentPropagation" : true, "allowEdgeOverflow" : false});
        }
        {
            var Q0;
            Q0=makeQuery(id+"F13.boolean.opBoolean","MERGE",FACE,{"derivedFrom":[makeQuery(id+"F1.opExtrude","SWEPT_FACE",FACE,{"disambiguationData":[OSD([sQuery(id+"F0.wireOp",EDGE,"E8.trimOffspring")])]}),makeQuery(id+"F13.opExtrude","SWEPT_FACE",FACE,{"disambiguationData":[OSD([sQuery(id+"F12.wireOp",EDGE,"E92")])]})]});
            var sketch = newSketch(context, id + "F15", { "sketchPlane" : qUnion([Q0])});
            skLineSegment(sketch, "E94.bottom", {"start": v(1970, -1262.8) * mm, "end": v(170, -1262.8) * mm});
            skLineSegment(sketch, "E94.top", {"start": v(1970, 587.2) * mm, "end": v(170, 587.2) * mm});
            skLineSegment(sketch, "E94.left", {"start": v(1970, -1262.8) * mm, "end": v(1970, 587.2) * mm});
            skLineSegment(sketch, "E94.right", {"start": v(170, -1262.8) * mm, "end": v(170, 587.2) * mm});
            skLineSegment(sketch, "E95", {"start": v(1070, 1672.86) * mm, "end": v(1070, -2259.53) * mm, "construction": true});
            skSolve(sketch);
        }
        {
            var Q0;
            {var subQ0=sQuery(id+"F15.wireOp",EDGE,"E94.top");Q0=makeQuery(id+"F15.imprint","IMPRINT",FACE,{"disambiguationData":[TD([[makeQuery(id+"F15.imprint","IMPRINT",EDGE,{"derivedFrom":subQ0}),1.0]])]});}
            var Q1;
            {var subQ0=sQuery(id+"F15.wireOp",EDGE,"E94.bottom");Q1=makeQuery(id+"F15.imprint","IMPRINT",FACE,{"disambiguationData":[TD([[makeQuery(id+"F15.imprint","IMPRINT",EDGE,{"derivedFrom":subQ0}),-1.0]])]});}
            var Q2;
            {var subQ0=sQuery(id+"F15.wireOp",EDGE,"E94.left");var subQ1=makeQuery(id+"F1.opExtrude","SWEPT_EDGE",EDGE,{"disambiguationData":[OSD([sQuery(id+"F0.wireOp",EDGE,"E1"),sQuery(id+"F0.wireOp",EDGE,"E8.trimOffspring")])]});var subQ2=makeQuery(id+"F15.imprint","INTERSECT",VERTEX,{"derivedFrom":[subQ1,subQ0]});Q2=makeQuery(id+"F15.imprint","IMPRINT",FACE,{"disambiguationData":[TD([[makeQuery(id+"F15.imprint","IMPRINT",EDGE,{"disambiguationData":[TD([[subQ2,-1.0]])],"derivedFrom":subQ0}),1.0]])]});}
            extrude(context, id + "F16", {"entities" : qUnion([Q0, Q1, Q2]), "operationType" : NewBodyOperationType.REMOVE, "oppositeDirection" : true, "depth" : 200 * mm});
        }
        {
            var Q0;
            Q0=makeQuery(id+"F1.opExtrude","SWEPT_FACE",FACE,{"disambiguationData":[OSD([sQuery(id+"F0.wireOp",EDGE,"E1")])]});
            var sketch = newSketch(context, id + "F17", { "sketchPlane" : qUnion([Q0])});
            skLineSegment(sketch, "E96", {"start": v(-1901.52, 811.14) * mm, "end": v(-238.48, 811.14) * mm});
            skLineSegment(sketch, "E97", {"start": v(-188.64, 765.13) * mm, "end": v(-150.24, 285.13) * mm});
            skLineSegment(sketch, "E98", {"start": v(-200.08, 231.14) * mm, "end": v(-1939.92, 231.14) * mm});
            skLineSegment(sketch, "E99", {"start": v(-1989.76, 285.13) * mm, "end": v(-1951.36, 765.13) * mm});
            skPoint(sketch, "E100.visualSharp", {"position": v(-1947.68, 811.14) * mm});
            skArc(sketch, "E100.filletArc", {"start": v(-1901.52, 811.14) * mm, "mid": v(-1935.44, 797.88) * mm, "end": v(-1951.36, 765.13) * mm});
            skPoint(sketch, "E101.visualSharp", {"position": v(-1994.08, 231.14) * mm});
            skArc(sketch, "E101.filletArc", {"start": v(-1989.76, 285.13) * mm, "mid": v(-1976.66, 247.23) * mm, "end": v(-1939.92, 231.14) * mm});
            skPoint(sketch, "E102.visualSharp", {"position": v(-145.92, 231.14) * mm});
            skArc(sketch, "E102.filletArc", {"start": v(-200.08, 231.14) * mm, "mid": v(-163.34, 247.23) * mm, "end": v(-150.24, 285.13) * mm});
            skPoint(sketch, "E103.visualSharp", {"position": v(-192.32, 811.14) * mm});
            skArc(sketch, "E103.filletArc", {"start": v(-188.64, 765.13) * mm, "mid": v(-204.56, 797.88) * mm, "end": v(-238.48, 811.14) * mm});
            skSolve(sketch);
        }
        {
            var Q0;
            Q0=makeQuery(id+"F17.imprint","IMPRINT",FACE,{"disambiguationData":[TD([[makeQuery(id+"F17.imprint","IMPRINT",EDGE,{"derivedFrom":sQuery(id+"F17.wireOp",EDGE,"E96")}),-1.0]])]});
            extrude(context, id + "F18", {"entities" : qUnion([Q0]), "operationType" : NewBodyOperationType.REMOVE, "oppositeDirection" : true, "depth" : 25 * mm});
        }
        {
            var Q0;
            Q0=makeQuery(id+"F9.boolean.opBoolean","SPLIT",FACE,{"disambiguationData":[TD([makeQuery(id+"F3.boolean.opBoolean","COPY",FACE,{"derivedFrom":makeQuery(id+"F3.opExtrude","SWEPT_FACE",FACE,{"disambiguationData":[OSD([sQuery(id+"F2.wireOp",EDGE,"E11")])]})}),makeQuery(id+"F9.opExtrude","SWEPT_FACE",FACE,{"disambiguationData":[OSD([sQuery(id+"F8.wireOp",EDGE,"E53")])]}),makeQuery(id+"F9.opExtrude","SWEPT_FACE",FACE,{"disambiguationData":[OSD([sQuery(id+"F8.wireOp",EDGE,"E54")])]}),makeQuery(id+"F9.opExtrude","SWEPT_FACE",FACE,{"disambiguationData":[OSD([sQuery(id+"F8.wireOp",EDGE,"E55")])]}),makeQuery(id+"F9.opExtrude","SWEPT_FACE",FACE,{"disambiguationData":[OSD([sQuery(id+"F8.wireOp",EDGE,"E56")])]}),makeQuery(id+"F9.opExtrude","SWEPT_FACE",FACE,{"disambiguationData":[OSD([sQuery(id+"F8.wireOp",EDGE,"E58")])]}),makeQuery(id+"F9.opExtrude","SWEPT_FACE",FACE,{"disambiguationData":[OSD([sQuery(id+"F8.wireOp",EDGE,"E60")])]}),makeQuery(id+"F9.opExtrude","SWEPT_FACE",FACE,{"disambiguationData":[OSD([sQuery(id+"F8.wireOp",EDGE,"E61")])]}),makeQuery(id+"F9.opExtrude","SWEPT_FACE",FACE,{"disambiguationData":[OSD([sQuery(id+"F8.wireOp",EDGE,"E62")])]}),makeQuery(id+"F9.opExtrude","SWEPT_FACE",FACE,{"disambiguationData":[OSD([sQuery(id+"F8.wireOp",EDGE,"E63")])]}),makeQuery(id+"F9.opExtrude","SWEPT_FACE",FACE,{"disambiguationData":[OSD([sQuery(id+"F8.wireOp",EDGE,"E64.filletArc")])]}),makeQuery(id+"F9.opExtrude","SWEPT_FACE",FACE,{"disambiguationData":[OSD([sQuery(id+"F8.wireOp",EDGE,"E65.filletArc")])]}),makeQuery(id+"F9.opExtrude","SWEPT_FACE",FACE,{"disambiguationData":[OSD([sQuery(id+"F8.wireOp",EDGE,"E66.filletArc")])]}),makeQuery(id+"F9.opExtrude","SWEPT_FACE",FACE,{"disambiguationData":[OSD([sQuery(id+"F8.wireOp",EDGE,"E67.filletArc")])]})])],"derivedFrom":makeQuery(id+"F3.boolean.opBoolean","COPY",FACE,{"derivedFrom":makeQuery(id+"F3.opExtrude","SWEPT_FACE",FACE,{"disambiguationData":[OSD([sQuery(id+"F2.wireOp",EDGE,"E12")])]})})});
            var sketch = newSketch(context, id + "F19", { "sketchPlane" : qUnion([Q0])});
            skLineSegment(sketch, "E104.bottom", {"start": v(1042.8, 5.56) * mm, "end": v(892.8, 5.56) * mm});
            skLineSegment(sketch, "E104.top", {"start": v(1042.8, -44.44) * mm, "end": v(892.8, -44.44) * mm});
            skLineSegment(sketch, "E104.left", {"start": v(1042.8, 5.56) * mm, "end": v(1042.8, -44.44) * mm});
            skLineSegment(sketch, "E104.right", {"start": v(892.8, 5.56) * mm, "end": v(892.8, -44.44) * mm});
            skSolve(sketch);
        }
        {
            var Q0;
            Q0=makeQuery(id+"F19.imprint","IMPRINT",FACE,{"disambiguationData":[TD([[makeQuery(id+"F19.imprint","IMPRINT",EDGE,{"derivedFrom":sQuery(id+"F19.wireOp",EDGE,"E104.bottom")}),1.0]])]});
            extrude(context, id + "F20", {"entities" : qUnion([Q0]), "operationType" : NewBodyOperationType.ADD, "depth" : 40 * mm});
        }
        {
            var Q0;
            Q0=makeQuery(id+"F11.boolean.opBoolean","SPLIT",FACE,{"disambiguationData":[TD([makeQuery(id+"F3.boolean.opBoolean","COPY",FACE,{"derivedFrom":makeQuery(id+"F3.opExtrude","SWEPT_FACE",FACE,{"disambiguationData":[OSD([sQuery(id+"F2.wireOp",EDGE,"E17")])]})}),makeQuery(id+"F11.opExtrude","SWEPT_FACE",FACE,{"disambiguationData":[OSD([sQuery(id+"F10.wireOp",EDGE,"E70.MirrorCS")])]}),makeQuery(id+"F11.opExtrude","SWEPT_FACE",FACE,{"disambiguationData":[OSD([sQuery(id+"F10.wireOp",EDGE,"E71.MirrorCS")])]}),makeQuery(id+"F11.opExtrude","SWEPT_FACE",FACE,{"disambiguationData":[OSD([sQuery(id+"F10.wireOp",EDGE,"E72.MirrorCS")])]}),makeQuery(id+"F11.opExtrude","SWEPT_FACE",FACE,{"disambiguationData":[OSD([sQuery(id+"F10.wireOp",EDGE,"E73.MirrorCS")])]}),makeQuery(id+"F11.opExtrude","SWEPT_FACE",FACE,{"disambiguationData":[OSD([sQuery(id+"F10.wireOp",EDGE,"E75.MirrorCS")])]}),makeQuery(id+"F11.opExtrude","SWEPT_FACE",FACE,{"disambiguationData":[OSD([sQuery(id+"F10.wireOp",EDGE,"E81")])]}),makeQuery(id+"F11.opExtrude","SWEPT_FACE",FACE,{"disambiguationData":[OSD([sQuery(id+"F10.wireOp",EDGE,"E82")])]}),makeQuery(id+"F11.opExtrude","SWEPT_FACE",FACE,{"disambiguationData":[OSD([sQuery(id+"F10.wireOp",EDGE,"E83")])]}),makeQuery(id+"F11.opExtrude","SWEPT_FACE",FACE,{"disambiguationData":[OSD([sQuery(id+"F10.wireOp",EDGE,"E84")])]}),makeQuery(id+"F11.opExtrude","SWEPT_FACE",FACE,{"disambiguationData":[OSD([sQuery(id+"F10.wireOp",EDGE,"E85.filletArc")])]}),makeQuery(id+"F11.opExtrude","SWEPT_FACE",FACE,{"disambiguationData":[OSD([sQuery(id+"F10.wireOp",EDGE,"E86.filletArc")])]}),makeQuery(id+"F11.opExtrude","SWEPT_FACE",FACE,{"disambiguationData":[OSD([sQuery(id+"F10.wireOp",EDGE,"E87.filletArc")])]}),makeQuery(id+"F11.opExtrude","SWEPT_FACE",FACE,{"disambiguationData":[OSD([sQuery(id+"F10.wireOp",EDGE,"E88.filletArc")])]})])],"derivedFrom":makeQuery(id+"F3.boolean.opBoolean","COPY",FACE,{"derivedFrom":makeQuery(id+"F3.opExtrude","SWEPT_FACE",FACE,{"disambiguationData":[OSD([sQuery(id+"F2.wireOp",EDGE,"E18")])]})})});
            var sketch = newSketch(context, id + "F21", { "sketchPlane" : qUnion([Q0])});
            skLineSegment(sketch, "E105.bottom", {"start": v(-1042.8, 176.21) * mm, "end": v(-892.8, 176.21) * mm});
            skLineSegment(sketch, "E105.top", {"start": v(-1042.8, 126.21) * mm, "end": v(-892.8, 126.21) * mm});
            skLineSegment(sketch, "E105.left", {"start": v(-1042.8, 176.21) * mm, "end": v(-1042.8, 126.21) * mm});
            skLineSegment(sketch, "E105.right", {"start": v(-892.8, 176.21) * mm, "end": v(-892.8, 126.21) * mm});
            skSolve(sketch);
        }
        {
            var Q0;
            Q0=makeQuery(id+"F21.imprint","IMPRINT",FACE,{"disambiguationData":[TD([[makeQuery(id+"F21.imprint","IMPRINT",EDGE,{"derivedFrom":sQuery(id+"F21.wireOp",EDGE,"E105.bottom")}),-1.0]])]});
            extrude(context, id + "F22", {"entities" : qUnion([Q0]), "operationType" : NewBodyOperationType.ADD, "depth" : 40 * mm});
        }
        {
            var Q0;
            Q0=makeQuery(id+"F20.opExtrude","CAP_EDGE",EDGE,{"disambiguationData":[OSD([sQuery(id+"F19.wireOp",EDGE,"E104.left")])],"isStart":false});
            var Q1;
            Q1=makeQuery(id+"F20.opExtrude","CAP_EDGE",EDGE,{"disambiguationData":[OSD([sQuery(id+"F19.wireOp",EDGE,"E104.right")])],"isStart":false});
            var Q2;
            Q2=makeQuery(id+"F22.opExtrude","CAP_EDGE",EDGE,{"disambiguationData":[OSD([sQuery(id+"F21.wireOp",EDGE,"E105.right")])],"isStart":false});
            var Q3;
            Q3=makeQuery(id+"F22.opExtrude","CAP_EDGE",EDGE,{"disambiguationData":[OSD([sQuery(id+"F21.wireOp",EDGE,"E105.left")])],"isStart":false});
            fillet(context, id + "F23", {"entities" : qUnion([Q0, Q1, Q2, Q3]), "radius" : 25 * mm, "tangentPropagation" : true, "allowEdgeOverflow" : false});
        }
        {
            var Q0;
            Q0=makeQuery(id+"F20.opExtrude","SWEPT_EDGE",EDGE,{"disambiguationData":[OSD([sQuery(id+"F19.wireOp",EDGE,"E104.bottom"),sQuery(id+"F19.wireOp",EDGE,"E104.left")])]});
            var Q1;
            Q1=makeQuery(id+"F20.opExtrude","CAP_EDGE",EDGE,{"disambiguationData":[OSD([sQuery(id+"F19.wireOp",EDGE,"E104.top")])],"isStart":false});
            var Q2;
            Q2=makeQuery(id+"F22.opExtrude","CAP_EDGE",EDGE,{"disambiguationData":[OSD([sQuery(id+"F21.wireOp",EDGE,"E105.bottom")])],"isStart":false});
            var Q3;
            Q3=makeQuery(id+"F22.opExtrude","CAP_EDGE",EDGE,{"disambiguationData":[OSD([sQuery(id+"F21.wireOp",EDGE,"E105.top")])],"isStart":false});
            chamfer(context, id + "F24", {"entities" : qUnion([Q0, Q1, Q2, Q3]), "width" : 12.5 * mm, "tangentPropagation" : true});
        }
        {
            var Q0;
            {var subQ0=makeQuery(id+"F3.boolean.opBoolean","COPY",FACE,{"derivedFrom":makeQuery(id+"F3.opExtrude","SWEPT_FACE",FACE,{"disambiguationData":[OSD([sQuery(id+"F2.wireOp",EDGE,"E12")])]})});Q0=makeQuery(id+"F14.opFillet","SPLIT",FACE,{"disambiguationData":[OD(0.0)],"derivedFrom":makeQuery(id+"F9.boolean.opBoolean","SPLIT",FACE,{"disambiguationData":[TD([makeQuery(id+"F1.opExtrude","SWEPT_FACE",FACE,{"disambiguationData":[OSD([sQuery(id+"F0.wireOp",EDGE,"E1")])]}),makeQuery(id+"F1.opExtrude","SWEPT_FACE",FACE,{"disambiguationData":[OSD([sQuery(id+"F0.wireOp",EDGE,"E2")])]}),makeQuery(id+"F1.opExtrude","SWEPT_FACE",FACE,{"disambiguationData":[OSD([sQuery(id+"F0.wireOp",EDGE,"E3")])]}),makeQuery(id+"F1.opExtrude","SWEPT_FACE",FACE,{"disambiguationData":[OSD([sQuery(id+"F0.wireOp",EDGE,"E4")])]}),makeQuery(id+"F1.opExtrude","SWEPT_FACE",FACE,{"disambiguationData":[OSD([sQuery(id+"F0.wireOp",EDGE,"E5")])]}),makeQuery(id+"F1.opExtrude","SWEPT_FACE",FACE,{"disambiguationData":[OSD([sQuery(id+"F0.wireOp",EDGE,"E6")])]}),makeQuery(id+"F3.boolean.opBoolean","COPY",FACE,{"derivedFrom":makeQuery(id+"F3.opExtrude","SWEPT_FACE",FACE,{"disambiguationData":[OSD([sQuery(id+"F2.wireOp",EDGE,"E11")])]})}),subQ0,makeQuery(id+"F9.opExtrude","SWEPT_FACE",FACE,{"disambiguationData":[OSD([sQuery(id+"F8.wireOp",EDGE,"E47")])]}),makeQuery(id+"F9.opExtrude","SWEPT_FACE",FACE,{"disambiguationData":[OSD([sQuery(id+"F8.wireOp",EDGE,"E48")])]}),makeQuery(id+"F9.opExtrude","SWEPT_FACE",FACE,{"disambiguationData":[OSD([sQuery(id+"F8.wireOp",EDGE,"E49")])]}),makeQuery(id+"F9.opExtrude","SWEPT_FACE",FACE,{"disambiguationData":[OSD([sQuery(id+"F8.wireOp",EDGE,"E50")])]}),makeQuery(id+"F9.opExtrude","SWEPT_FACE",FACE,{"disambiguationData":[OSD([sQuery(id+"F8.wireOp",EDGE,"E52")])]})])],"derivedFrom":subQ0})});}
            var sketch = newSketch(context, id + "F25", { "sketchPlane" : qUnion([Q0])});
            skLineSegment(sketch, "E106", {"start": v(127.49, 671.7) * mm, "end": v(-105.25, -300.84) * mm, "construction": true});
            skPoint(sketch, "E106.startSnap0", {"position": v(127.53, 671.7) * mm});
            skLineSegment(sketch, "E107.bottom", {"start": v(97.88, 601.68) * mm, "end": v(122.2, 595.86) * mm});
            skLineSegment(sketch, "E107.top", {"start": v(-18.5, 115.41) * mm, "end": v(5.82, 109.6) * mm});
            skLineSegment(sketch, "E107.left", {"start": v(97.88, 601.68) * mm, "end": v(-18.5, 115.41) * mm});
            skLineSegment(sketch, "E107.right", {"start": v(122.2, 595.86) * mm, "end": v(5.82, 109.6) * mm});
            skSolve(sketch);
        }
        {
            var Q0;
            {var subQ0=makeQuery(id+"F3.boolean.opBoolean","COPY",FACE,{"derivedFrom":makeQuery(id+"F3.opExtrude","SWEPT_FACE",FACE,{"disambiguationData":[OSD([sQuery(id+"F2.wireOp",EDGE,"E18")])]})});Q0=makeQuery(id+"F14.opFillet","SPLIT",FACE,{"disambiguationData":[OD(0.0)],"derivedFrom":makeQuery(id+"F11.boolean.opBoolean","SPLIT",FACE,{"disambiguationData":[TD([makeQuery(id+"F1.opExtrude","SWEPT_FACE",FACE,{"disambiguationData":[OSD([sQuery(id+"F0.wireOp",EDGE,"E1")])]}),makeQuery(id+"F1.opExtrude","SWEPT_FACE",FACE,{"disambiguationData":[OSD([sQuery(id+"F0.wireOp",EDGE,"E2")])]}),makeQuery(id+"F1.opExtrude","SWEPT_FACE",FACE,{"disambiguationData":[OSD([sQuery(id+"F0.wireOp",EDGE,"E3")])]}),makeQuery(id+"F1.opExtrude","SWEPT_FACE",FACE,{"disambiguationData":[OSD([sQuery(id+"F0.wireOp",EDGE,"E4")])]}),makeQuery(id+"F1.opExtrude","SWEPT_FACE",FACE,{"disambiguationData":[OSD([sQuery(id+"F0.wireOp",EDGE,"E5")])]}),makeQuery(id+"F1.opExtrude","SWEPT_FACE",FACE,{"disambiguationData":[OSD([sQuery(id+"F0.wireOp",EDGE,"E6")])]}),makeQuery(id+"F3.boolean.opBoolean","COPY",FACE,{"derivedFrom":makeQuery(id+"F3.opExtrude","SWEPT_FACE",FACE,{"disambiguationData":[OSD([sQuery(id+"F2.wireOp",EDGE,"E17")])]})}),subQ0,makeQuery(id+"F11.opExtrude","SWEPT_FACE",FACE,{"disambiguationData":[OSD([sQuery(id+"F10.wireOp",EDGE,"E69.MirrorCS")])]}),makeQuery(id+"F11.opExtrude","SWEPT_FACE",FACE,{"disambiguationData":[OSD([sQuery(id+"F10.wireOp",EDGE,"E77.MirrorCS")])]}),makeQuery(id+"F11.opExtrude","SWEPT_FACE",FACE,{"disambiguationData":[OSD([sQuery(id+"F10.wireOp",EDGE,"E78.MirrorCS")])]}),makeQuery(id+"F11.opExtrude","SWEPT_FACE",FACE,{"disambiguationData":[OSD([sQuery(id+"F10.wireOp",EDGE,"E79.MirrorCS")])]}),makeQuery(id+"F11.opExtrude","SWEPT_FACE",FACE,{"disambiguationData":[OSD([sQuery(id+"F10.wireOp",EDGE,"E80.MirrorCS")])]})])],"derivedFrom":subQ0})});}
            var sketch = newSketch(context, id + "F26", { "sketchPlane" : qUnion([Q0])});
            skLineSegment(sketch, "E108", {"start": v(-127.49, 842.36) * mm, "end": v(100.41, -109.97) * mm, "construction": true});
            skLineSegment(sketch, "E109.bottom", {"start": v(-97.87, 772.33) * mm, "end": v(-122.19, 766.5) * mm});
            skLineSegment(sketch, "E109.top", {"start": v(18.5, 286.06) * mm, "end": v(-5.82, 280.24) * mm});
            skLineSegment(sketch, "E109.left", {"start": v(-97.87, 772.33) * mm, "end": v(18.5, 286.06) * mm});
            skLineSegment(sketch, "E109.right", {"start": v(-122.19, 766.5) * mm, "end": v(-5.82, 280.24) * mm});
            skSolve(sketch);
        }
        {
            var Q0;
            Q0=makeQuery(id+"F25.imprint","IMPRINT",FACE,{"disambiguationData":[TD([[makeQuery(id+"F25.imprint","IMPRINT",EDGE,{"derivedFrom":sQuery(id+"F25.wireOp",EDGE,"E107.bottom")}),-1.0]])]});
            extrude(context, id + "F27", {"entities" : qUnion([Q0]), "operationType" : NewBodyOperationType.REMOVE, "oppositeDirection" : true, "depth" : 25 * mm});
        }
        {
            var Q0;
            Q0=makeQuery(id+"F1.opExtrude","SWEPT_FACE",FACE,{"disambiguationData":[OSD([sQuery(id+"F0.wireOp",EDGE,"E5")])]});
            var sketch = newSketch(context, id + "F28", { "sketchPlane" : qUnion([Q0])});
            skLineSegment(sketch, "E110.bottom", {"start": v(2030, -552) * mm, "end": v(1780, -552) * mm});
            skLineSegment(sketch, "E110.top", {"start": v(2030, -587) * mm, "end": v(1780, -587) * mm});
            skLineSegment(sketch, "E110.left", {"start": v(2030, -552) * mm, "end": v(2030, -587) * mm});
            skLineSegment(sketch, "E110.right", {"start": v(1780, -552) * mm, "end": v(1780, -587) * mm});
            skLineSegment(sketch, "E111.bottom", {"start": v(1780, -482) * mm, "end": v(2030, -482) * mm});
            skLineSegment(sketch, "E111.top", {"start": v(1780, -517) * mm, "end": v(2030, -517) * mm});
            skLineSegment(sketch, "E111.left", {"start": v(1780, -482) * mm, "end": v(1780, -517) * mm});
            skLineSegment(sketch, "E111.right", {"start": v(2030, -482) * mm, "end": v(2030, -517) * mm});
            skLineSegment(sketch, "E112", {"start": v(2030, -960.28) * mm, "end": v(2030, -222.9) * mm, "construction": true});
            skLineSegment(sketch, "E113.bottom", {"start": v(1480, -517) * mm, "end": v(1230, -517) * mm});
            skLineSegment(sketch, "E113.top", {"start": v(1480, -482) * mm, "end": v(1230, -482) * mm});
            skLineSegment(sketch, "E113.left", {"start": v(1480, -517) * mm, "end": v(1480, -482) * mm});
            skLineSegment(sketch, "E113.right", {"start": v(1230, -517) * mm, "end": v(1230, -482) * mm});
            skLineSegment(sketch, "E114.bottom", {"start": v(1230, -552) * mm, "end": v(1480, -552) * mm});
            skLineSegment(sketch, "E114.top", {"start": v(1230, -587) * mm, "end": v(1480, -587) * mm});
            skLineSegment(sketch, "E114.left", {"start": v(1230, -552) * mm, "end": v(1230, -587) * mm});
            skLineSegment(sketch, "E114.right", {"start": v(1480, -552) * mm, "end": v(1480, -587) * mm});
            skLineSegment(sketch, "E115.bottom", {"start": v(1505, -512) * mm, "end": v(1755, -512) * mm});
            skLineSegment(sketch, "E115.top", {"start": v(1505, -562) * mm, "end": v(1755, -562) * mm});
            skLineSegment(sketch, "E115.left", {"start": v(1505, -512) * mm, "end": v(1505, -562) * mm});
            skLineSegment(sketch, "E115.right", {"start": v(1755, -512) * mm, "end": v(1755, -562) * mm});
            skSolve(sketch);
        }
        {
            var Q0;
            Q0=makeQuery(id+"F28.imprint","IMPRINT",FACE,{"disambiguationData":[TD([[makeQuery(id+"F28.imprint","IMPRINT",EDGE,{"derivedFrom":sQuery(id+"F28.wireOp",EDGE,"E110.bottom")}),1.0]])]});
            var Q1;
            Q1=makeQuery(id+"F28.imprint","IMPRINT",FACE,{"disambiguationData":[TD([[makeQuery(id+"F28.imprint","IMPRINT",EDGE,{"derivedFrom":sQuery(id+"F28.wireOp",EDGE,"E111.bottom")}),-1.0]])]});
            var Q2;
            Q2=makeQuery(id+"F28.imprint","IMPRINT",FACE,{"disambiguationData":[TD([[makeQuery(id+"F28.imprint","IMPRINT",EDGE,{"derivedFrom":sQuery(id+"F28.wireOp",EDGE,"E113.bottom")}),-1.0]])]});
            var Q3;
            Q3=makeQuery(id+"F28.imprint","IMPRINT",FACE,{"disambiguationData":[TD([[makeQuery(id+"F28.imprint","IMPRINT",EDGE,{"derivedFrom":sQuery(id+"F28.wireOp",EDGE,"E114.bottom")}),-1.0]])]});
            extrude(context, id + "F29", {"entities" : qUnion([Q0, Q1, Q2, Q3]), "operationType" : NewBodyOperationType.REMOVE, "oppositeDirection" : true, "depth" : 25 * mm});
        }
        {
            var Q0;
            Q0=makeQuery(id+"F28.imprint","IMPRINT",FACE,{"disambiguationData":[TD([[makeQuery(id+"F28.imprint","IMPRINT",EDGE,{"derivedFrom":sQuery(id+"F28.wireOp",EDGE,"E115.bottom")}),-1.0]])]});
            extrude(context, id + "F30", {"entities" : qUnion([Q0]), "operationType" : NewBodyOperationType.ADD, "depth" : 60 * mm});
        }
        {
            var Q0;
            Q0=makeQuery(id+"F30.opExtrude","CAP_EDGE",EDGE,{"disambiguationData":[OSD([sQuery(id+"F28.wireOp",EDGE,"E115.right")])],"isStart":false});
            var Q1;
            Q1=makeQuery(id+"F30.opExtrude","CAP_EDGE",EDGE,{"disambiguationData":[OSD([sQuery(id+"F28.wireOp",EDGE,"E115.left")])],"isStart":false});
            fillet(context, id + "F31", {"entities" : qUnion([Q0, Q1]), "radius" : 40 * mm, "tangentPropagation" : true, "allowEdgeOverflow" : false});
        }
        {
            var Q0;
            Q0=makeQuery(id+"F30.opExtrude","CAP_EDGE",EDGE,{"disambiguationData":[OSD([sQuery(id+"F28.wireOp",EDGE,"E115.top")])],"isStart":false});
            var Q1;
            Q1=makeQuery(id+"F30.opExtrude","CAP_EDGE",EDGE,{"disambiguationData":[OSD([sQuery(id+"F28.wireOp",EDGE,"E115.bottom")])],"isStart":false});
            chamfer(context, id + "F32", {"entities" : qUnion([Q0, Q1]), "width" : 15 * mm, "tangentPropagation" : true});
        }
        {
            var Q0;
            Q0=makeQuery(id+"F26.imprint","IMPRINT",FACE,{"disambiguationData":[TD([[makeQuery(id+"F26.imprint","IMPRINT",EDGE,{"derivedFrom":sQuery(id+"F26.wireOp",EDGE,"E109.bottom")}),1.0]])]});
            extrude(context, id + "F33", {"entities" : qUnion([Q0]), "operationType" : NewBodyOperationType.REMOVE, "oppositeDirection" : true, "depth" : 25 * mm});
        }
    });
